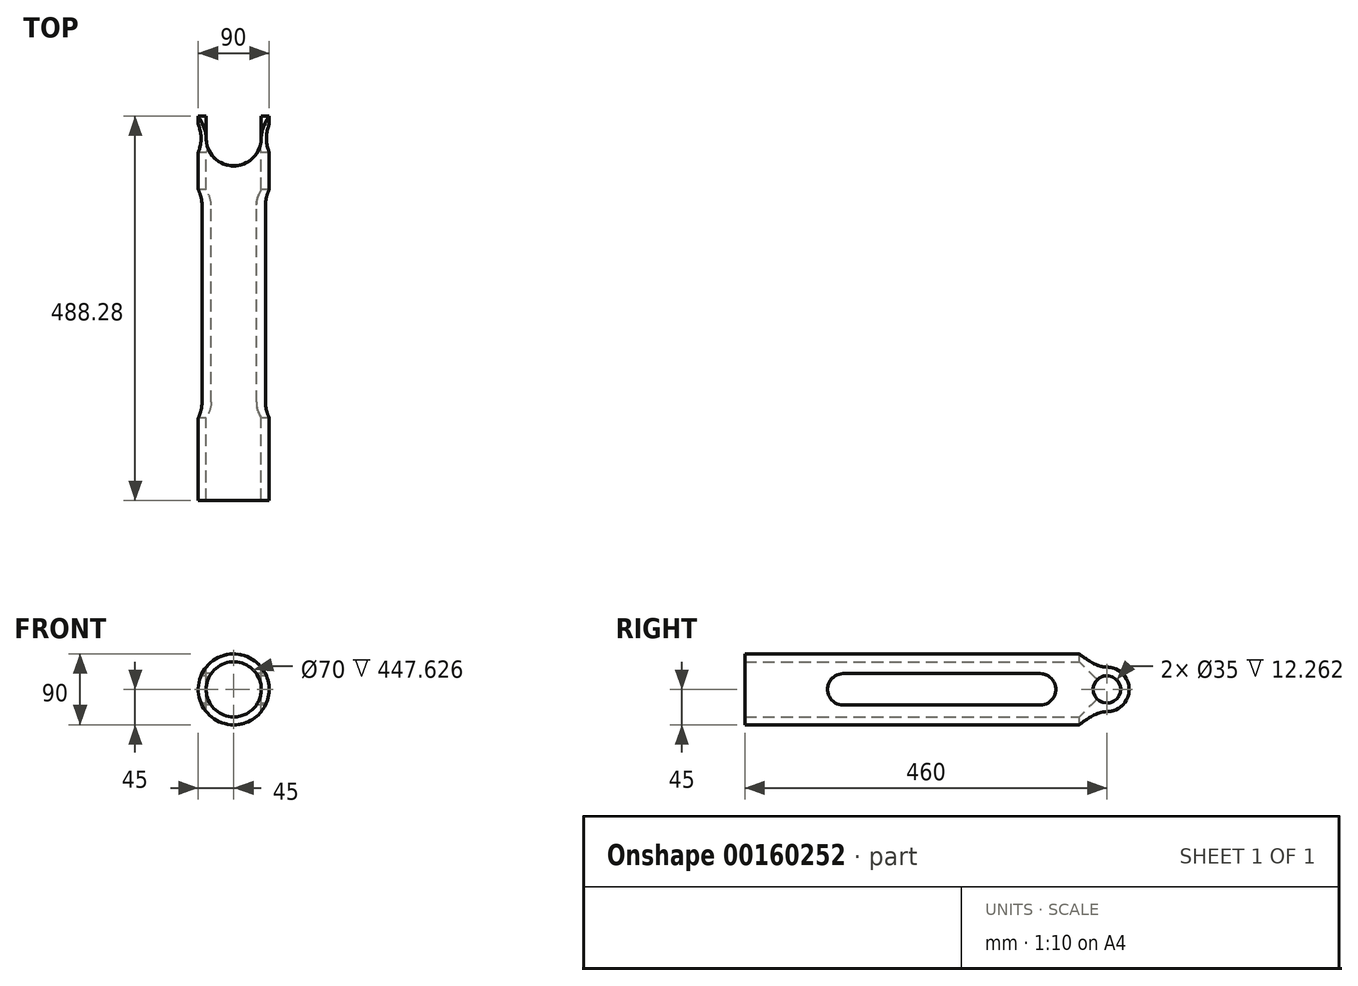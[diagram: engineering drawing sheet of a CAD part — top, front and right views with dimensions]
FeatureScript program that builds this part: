
annotation { "Feature Type Name" : "Feature", "Feature Type Description" : "" }
export const myFeature = defineFeature(function(context is Context, id is Id, definition is map)
    precondition{}
    {
        {
            var Q0;
            Q0=qCreatedBy(makeId("Front.planeOp"),FACE);
            var sketch = newSketch(context, id + "F0", { "sketchPlane" : qUnion([Q0])});
            skCircle(sketch, "E0", {"center": v(0, 0) * mm, "radius": 45 * mm});
            skCircle(sketch, "E1.0", {"center": v(0, 0) * mm, "radius": 35 * mm});
            skSolve(sketch);
        }
        {
            var Q0;
            Q0=makeQuery(id+"F0.imprint","IMPRINT",FACE,{"disambiguationData":[TD([[makeQuery(id+"F0.imprint","IMPRINT",EDGE,{"derivedFrom":sQuery(id+"F0.wireOp",EDGE,"E0")}),1.0]])]});
            extrude(context, id + "F1", {"entities" : qUnion([Q0]), "depth" : 500 * mm});
        }
        {
            var Q0;
            Q0=qCreatedBy(makeId("Right.planeOp"),FACE);
            var sketch = newSketch(context, id + "F2", { "sketchPlane" : qUnion([Q0])});
            skCircle(sketch, "E2", {"center": v(-125, 0) * mm, "radius": 20 * mm});
            skCircle(sketch, "E3", {"center": v(-375, 0) * mm, "radius": 20 * mm});
            skLineSegment(sketch, "E4", {"start": v(-375, 20) * mm, "end": v(-125, 20) * mm});
            skLineSegment(sketch, "E5", {"start": v(-375, -20) * mm, "end": v(-125, -20) * mm});
            skSolve(sketch);
        }
        {
            var Q0;
            Q0=qSketchRegion(id+"F2",true);
            extrude(context, id + "F3", {"entities" : qUnion([Q0]), "operationType" : NewBodyOperationType.REMOVE, "depth" : 200 * mm, "symmetric" : true});
        }
        {
            var Q0;
            Q0=qCreatedBy(makeId("Top.planeOp"),FACE);
            var sketch = newSketch(context, id + "F4", { "sketchPlane" : qUnion([Q0])});
            skArc(sketch, "E6", {"start": v(-35, -40) * mm, "mid": v(0, -75) * mm, "end": v(35, -40) * mm});
            skLineSegment(sketch, "E7", {"start": v(-35, -40) * mm, "end": v(-35, 0) * mm});
            skLineSegment(sketch, "E8", {"start": v(35, -40) * mm, "end": v(35, 0) * mm});
            skLineSegment(sketch, "E9", {"start": v(35, 0) * mm, "end": v(-35, 0) * mm});
            skSolve(sketch);
        }
        {
            var Q0;
            Q0=qSketchRegion(id+"F4",true);
            extrude(context, id + "F5", {"entities" : qUnion([Q0]), "operationType" : NewBodyOperationType.REMOVE, "oppositeDirection" : true, "depth" : 200 * mm, "symmetric" : true});
        }
        {
            var Q0;
            Q0=qCreatedBy(makeId("Right.planeOp"),FACE);
            var sketch = newSketch(context, id + "F6", { "sketchPlane" : qUnion([Q0])});
            skCircle(sketch, "E10", {"center": v(-40, 0) * mm, "radius": 17.5 * mm});
            skSolve(sketch);
        }
        {
            var Q0;
            Q0=qSketchRegion(id+"F6",true);
            extrude(context, id + "F7", {"entities" : qUnion([Q0]), "operationType" : NewBodyOperationType.REMOVE, "oppositeDirection" : true, "depth" : 200 * mm, "symmetric" : true});
        }
        {
            var Q0;
            Q0=makeQuery(id+"F5.boolean.opBoolean","COPY",FACE,{"derivedFrom":makeQuery(id+"F5.opExtrude","SWEPT_FACE",FACE,{"disambiguationData":[OSD([sQuery(id+"F4.wireOp",EDGE,"E7")])]})});
            var sketch = newSketch(context, id + "F8", { "sketchPlane" : qUnion([Q0])});
            skPoint(sketch, "E11", {"position": v(-40, 0) * mm});
            skArc(sketch, "E12", {"start": v(-40, -28.28) * mm, "mid": v(-11.72, 0) * mm, "end": v(-40, 28.28) * mm});
            skLineSegment(sketch, "E13", {"start": v(-40, 28.28) * mm, "end": v(0, 28.28) * mm});
            skLineSegment(sketch, "E14", {"start": v(0, 28.28) * mm, "end": v(0, -28.28) * mm});
            skLineSegment(sketch, "E15", {"start": v(0, -28.28) * mm, "end": v(-40, -28.28) * mm});
            skPoint(sketch, "E16", {"position": v(-22.5, 0) * mm});
            skSolve(sketch);
        }
        {
            var Q0;
            Q0=qSketchRegion(id+"F8",true);
            extrude(context, id + "F9", {"entities" : qUnion([Q0]), "operationType" : NewBodyOperationType.REMOVE, "oppositeDirection" : true, "depth" : 200 * mm, "symmetric" : true});
        }
        {
            var Q0;
            Q0=qCreatedBy(makeId("Front.planeOp"),FACE);
            var Q1;
            Q1=makeQuery(id+"F1.opExtrude","CAP_FACE",FACE,{"disambiguationData":[OSD([sQuery(id+"F0.wireOp",EDGE,"E0"),sQuery(id+"F0.wireOp",EDGE,"E1.0")])],"isStart":false});
            cPlane(context, id + "F10", {"entities" : qUnion([Q0, Q1]), "cplaneType" : CPlaneType.MID_PLANE, "offset" : 25 * mm, "width" : 150 * mm, "height" : 150 * mm});
        }
    });
